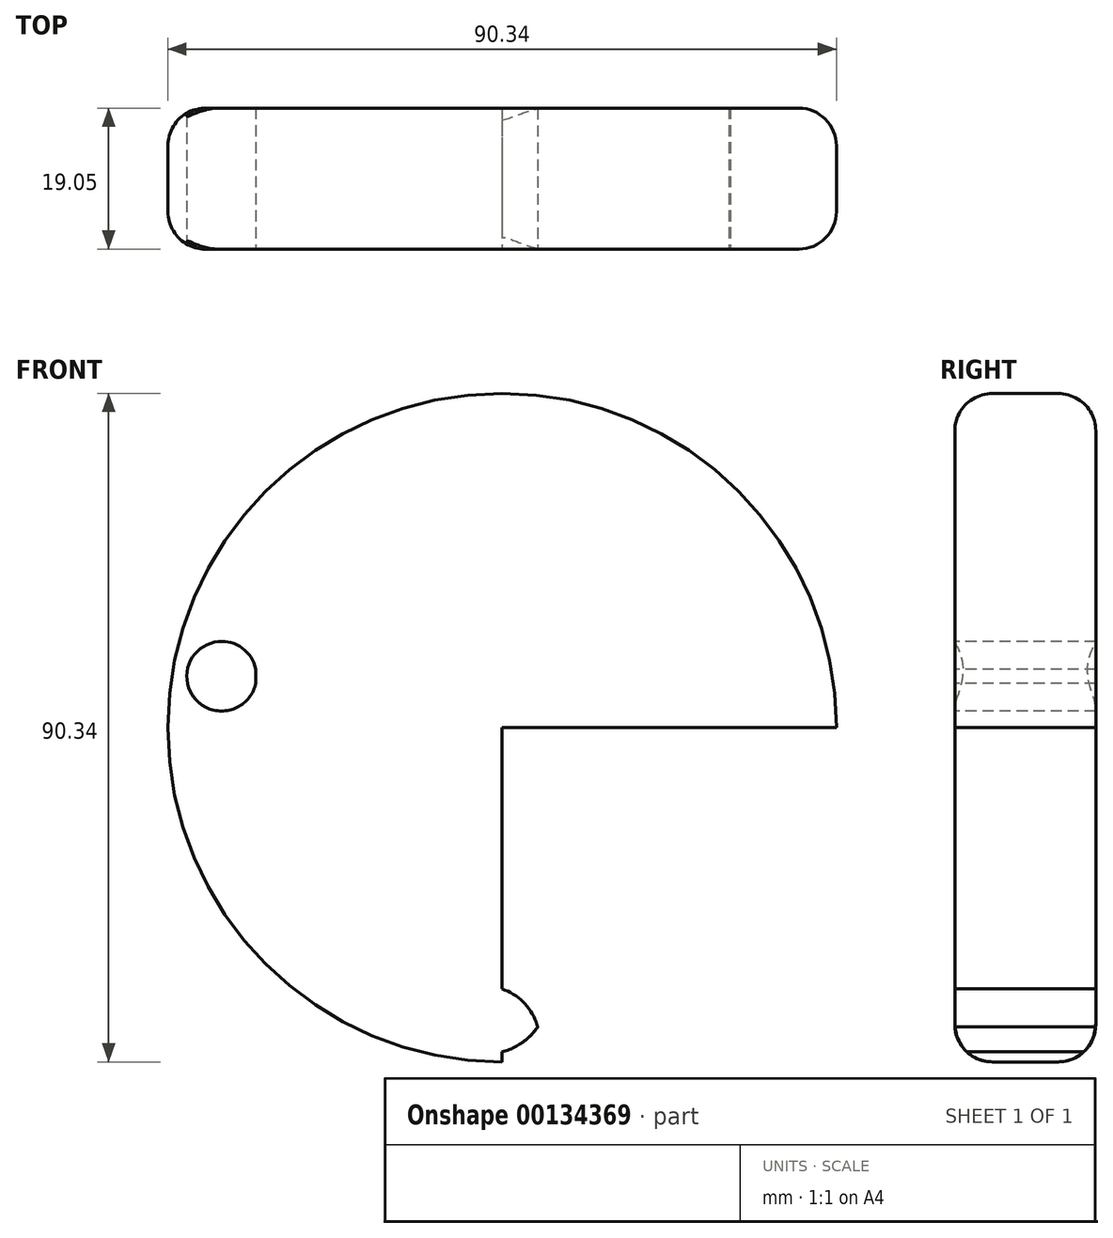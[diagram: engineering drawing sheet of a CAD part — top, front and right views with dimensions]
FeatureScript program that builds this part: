
annotation { "Feature Type Name" : "Feature", "Feature Type Description" : "" }
export const myFeature = defineFeature(function(context is Context, id is Id, definition is map)
    precondition{}
    {
        {
            var Q0;
            Q0=qCreatedBy(makeId("Front.planeOp"),FACE);
            var sketch = newSketch(context, id + "F0", { "sketchPlane" : qUnion([Q0])});
            skCircle(sketch, "E0", {"center": v(0, 0) * mm, "radius": 45.17 * mm});
            skLineSegment(sketch, "E1", {"start": v(0, 45.17) * mm, "end": v(0, -45.17) * mm});
            skLineSegment(sketch, "E2", {"start": v(45.17, 0) * mm, "end": v(-45.17, 0) * mm});
            skLineSegment(sketch, "E3", {"start": v(-4.8, 43) * mm, "end": v(-4.8, 30.65) * mm});
            skArc(sketch, "E4", {"start": v(7.34, 41.82) * mm, "mid": v(3.4, 43.95) * mm, "end": v(0, 41.03) * mm});
            skArc(sketch, "E5", {"start": v(1.47, 34.37) * mm, "mid": v(5.2, 37.46) * mm, "end": v(7.34, 41.82) * mm});
            skLineSegment(sketch, "E6", {"start": v(1.47, 34.37) * mm, "end": v(1.47, 30.65) * mm});
            skLineSegment(sketch, "E7", {"start": v(1.47, 30.65) * mm, "end": v(8.32, 30.65) * mm});
            skArc(sketch, "E8", {"start": v(0, -27.16) * mm, "mid": v(-6.53, -32.01) * mm, "end": v(-9.3, -39.66) * mm});
            skArc(sketch, "E9", {"start": v(-9.3, -39.66) * mm, "mid": v(-2.47, -44.04) * mm, "end": v(4.8, -40.45) * mm});
            skCircle(sketch, "E10", {"center": v(-37.9, 6.95) * mm, "radius": 4.7 * mm});
            skLineSegment(sketch, "E11", {"start": v(-33.3, 7.91) * mm, "end": v(-33.3, -5.58) * mm});
            skArc(sketch, "E12", {"start": v(39.07, 6.37) * mm, "mid": v(33.13, 11.92) * mm, "end": v(26.54, 7.15) * mm});
            skArc(sketch, "E13", {"start": v(30.65, 0) * mm, "mid": v(36.13, 1.5) * mm, "end": v(39.07, 6.37) * mm});
            skArc(sketch, "E14", {"start": v(37.5, -4.4) * mm, "mid": v(34.74, -1.17) * mm, "end": v(30.65, 0) * mm});
            skArc(sketch, "E15", {"start": v(27.32, -7.39) * mm, "mid": v(33.83, -10.73) * mm, "end": v(37.5, -4.4) * mm});
            skArc(sketch, "E16", {"start": v(4.8, -40.45) * mm, "mid": v(-1.97, -34.93) * mm, "end": v(-9.3, -39.66) * mm});
            skSolve(sketch);
        }
        {
            var Q0;
            {var subQ0=sQuery(id+"F0.wireOp",EDGE,"E1");var subQ1=sQuery(id+"F0.wireOp",EDGE,"E0");var subQ2=makeQuery(id+"F0.imprint","INTERSECT",VERTEX,{"disambiguationData":[OD(1.0)],"derivedFrom":[subQ1,subQ0]});Q0=makeQuery(id+"F0.imprint","IMPRINT",FACE,{"disambiguationData":[TD([[makeQuery(id+"F0.imprint","IMPRINT",EDGE,{"disambiguationData":[TD([[subQ2,-1.0]])],"derivedFrom":subQ1}),1.0]])]});}
            var Q1;
            {var subQ9=sQuery(id+"F0.wireOp",EDGE,"E8");Q1=makeQuery(id+"F0.imprint","IMPRINT",FACE,{"disambiguationData":[TD([[makeQuery(id+"F0.imprint","IMPRINT",EDGE,{"derivedFrom":subQ9}),-1.0]])]});}
            var Q2;
            {var subQ2=sQuery(id+"F0.wireOp",EDGE,"E1");var subQ4=makeQuery(id+"F0.imprint","IMPRINT",VERTEX,{"derivedFrom":subQ2});Q2=makeQuery(id+"F0.imprint","IMPRINT",FACE,{"disambiguationData":[TD([[makeQuery(id+"F0.imprint","IMPRINT",EDGE,{"disambiguationData":[TD([[subQ4,1.0]])],"derivedFrom":subQ2}),-1.0]])]});}
            var Q3;
            {var subQ5=sQuery(id+"F0.wireOp",EDGE,"E1");var subQ6=makeQuery(id+"F0.imprint","IMPRINT",VERTEX,{"derivedFrom":subQ5});Q3=makeQuery(id+"F0.imprint","IMPRINT",FACE,{"disambiguationData":[TD([[makeQuery(id+"F0.imprint","IMPRINT",EDGE,{"disambiguationData":[TD([[subQ6,1.0]])],"derivedFrom":subQ5}),1.0]])]});}
            var Q4;
            {var subQ0=sQuery(id+"F0.wireOp",EDGE,"E11");var subQ1=sQuery(id+"F0.wireOp",EDGE,"E10");var subQ2=makeQuery(id+"F0.imprint","INTERSECT",VERTEX,{"disambiguationData":[OD(0.0)],"derivedFrom":[subQ1,subQ0]});Q4=makeQuery(id+"F0.imprint","IMPRINT",FACE,{"disambiguationData":[TD([[makeQuery(id+"F0.imprint","IMPRINT",EDGE,{"disambiguationData":[TD([[subQ2,-1.0]])],"derivedFrom":subQ1}),1.0]])]});}
            var Q5;
            {var subQ0=sQuery(id+"F0.wireOp",EDGE,"E16");var subQ1=sQuery(id+"F0.wireOp",EDGE,"E1");var subQ2=makeQuery(id+"F0.imprint","INTERSECT",VERTEX,{"derivedFrom":[subQ1,subQ0]});Q5=makeQuery(id+"F0.imprint","IMPRINT",FACE,{"disambiguationData":[TD([[makeQuery(id+"F0.imprint","IMPRINT",EDGE,{"disambiguationData":[TD([[subQ2,-1.0]])],"derivedFrom":subQ1}),-1.0]])]});}
            var Q6;
            {var subQ0=sQuery(id+"F0.wireOp",EDGE,"E8");Q6=makeQuery(id+"F0.imprint","IMPRINT",FACE,{"disambiguationData":[TD([[makeQuery(id+"F0.imprint","IMPRINT",EDGE,{"derivedFrom":subQ0}),1.0]])]});}
            var Q7;
            {var subQ0=sQuery(id+"F0.wireOp",EDGE,"E16");var subQ1=sQuery(id+"F0.wireOp",EDGE,"E1");var subQ2=makeQuery(id+"F0.imprint","INTERSECT",VERTEX,{"derivedFrom":[subQ1,subQ0]});Q7=makeQuery(id+"F0.imprint","IMPRINT",FACE,{"disambiguationData":[TD([[makeQuery(id+"F0.imprint","IMPRINT",EDGE,{"disambiguationData":[TD([[subQ2,-1.0]])],"derivedFrom":subQ1}),1.0]])]});}
            extrude(context, id + "F1", {"entities" : qUnion([Q0, Q1, Q2, Q3, Q4, Q5, Q6, Q7]), "oppositeDirection" : true, "depth" : 19.05 * mm});
        }
        {
            var Q0;
            Q0=makeQuery(id+"F1.opExtrude","CAP_EDGE",EDGE,{"disambiguationData":[OSD([sQuery(id+"F0.wireOp",EDGE,"E0")])],"isStart":true});
            var Q1;
            Q1=makeQuery(id+"F1.opExtrude","CAP_EDGE",EDGE,{"disambiguationData":[OSD([sQuery(id+"F0.wireOp",EDGE,"E0")])],"isStart":false});
            fillet(context, id + "F2", {"entities" : qUnion([Q0, Q1]), "radius" : 5.08 * mm, "tangentPropagation" : true, "allowEdgeOverflow" : false});
        }
    });
